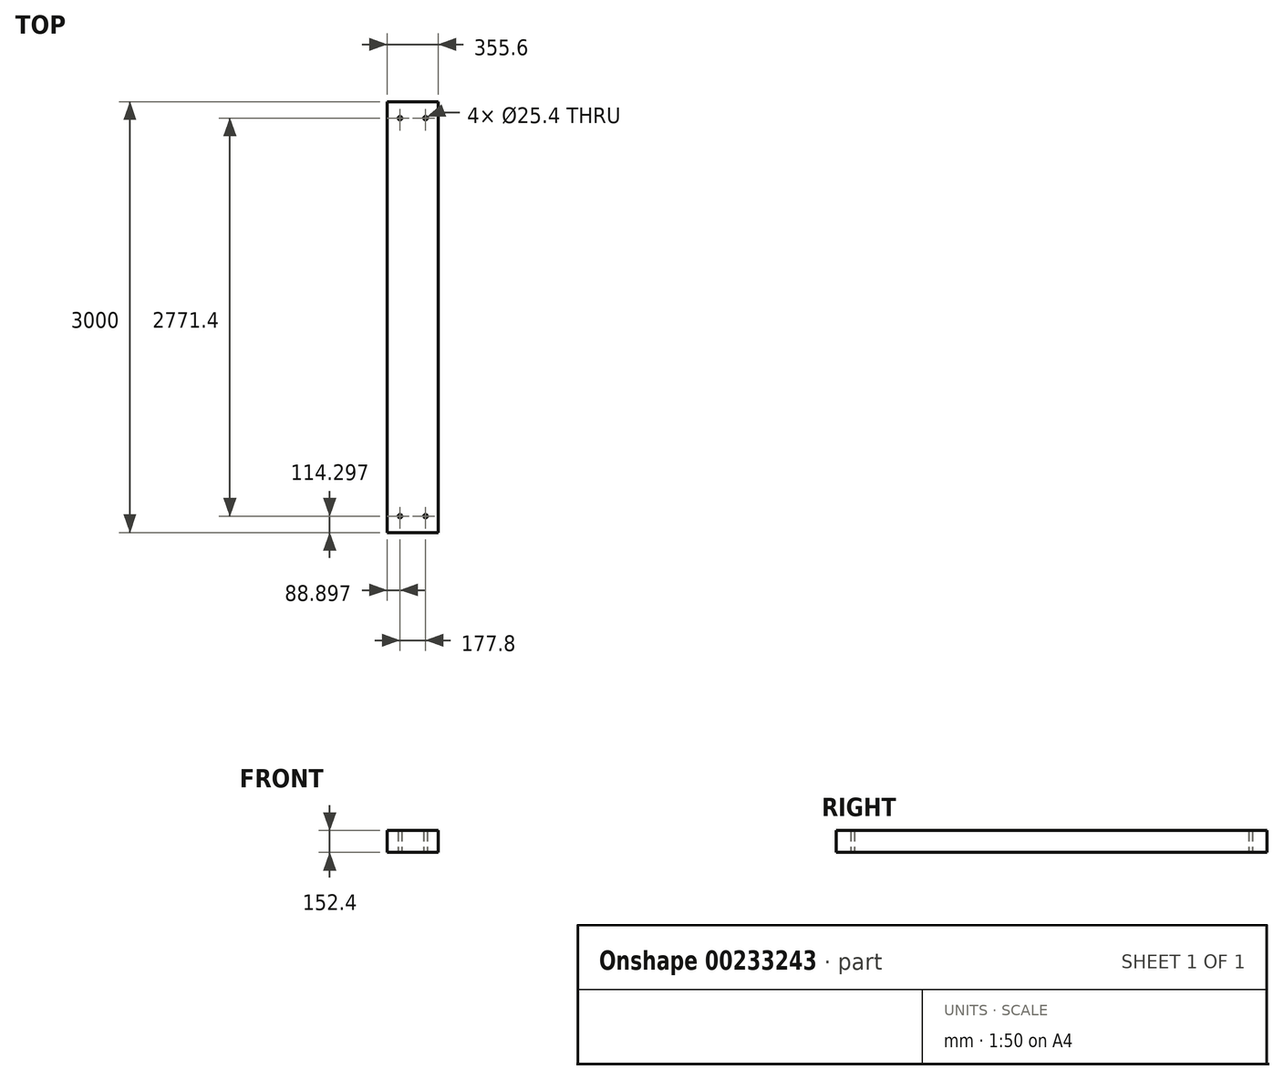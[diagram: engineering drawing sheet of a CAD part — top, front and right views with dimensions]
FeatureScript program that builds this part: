
annotation { "Feature Type Name" : "Feature", "Feature Type Description" : "" }
export const myFeature = defineFeature(function(context is Context, id is Id, definition is map)
    precondition{}
    {
        {
            var Q0;
            Q0=qCreatedBy(makeId("Top.planeOp"),FACE);
            var sketch = newSketch(context, id + "F0", { "sketchPlane" : qUnion([Q0])});
            skLineSegment(sketch, "E0.bottom", {"start": v(-343.64, 744.1) * mm, "end": v(-699.24, 744.1) * mm});
            skLineSegment(sketch, "E0.top", {"start": v(-343.64, -2255.9) * mm, "end": v(-699.24, -2255.9) * mm});
            skLineSegment(sketch, "E0.left", {"start": v(-343.64, 744.1) * mm, "end": v(-343.64, -2255.9) * mm});
            skLineSegment(sketch, "E0.right", {"start": v(-699.24, 744.1) * mm, "end": v(-699.24, -2255.9) * mm});
            skCircle(sketch, "E1", {"center": v(-610.34, -2141.6) * mm, "radius": 12.7 * mm});
            skCircle(sketch, "E2", {"center": v(-432.54, -2141.6) * mm, "radius": 12.7 * mm});
            skCircle(sketch, "E3", {"center": v(-610.34, 629.8) * mm, "radius": 12.7 * mm});
            skCircle(sketch, "E4", {"center": v(-432.54, 629.8) * mm, "radius": 12.7 * mm});
            skSolve(sketch);
        }
        {
            var Q0;
            Q0 = qSketchRegion(id + "F0", true);
            extrude(context, id + "F1", {"entities" : qUnion([Q0]), "depth" : 152.4 * mm});
        }
    });
